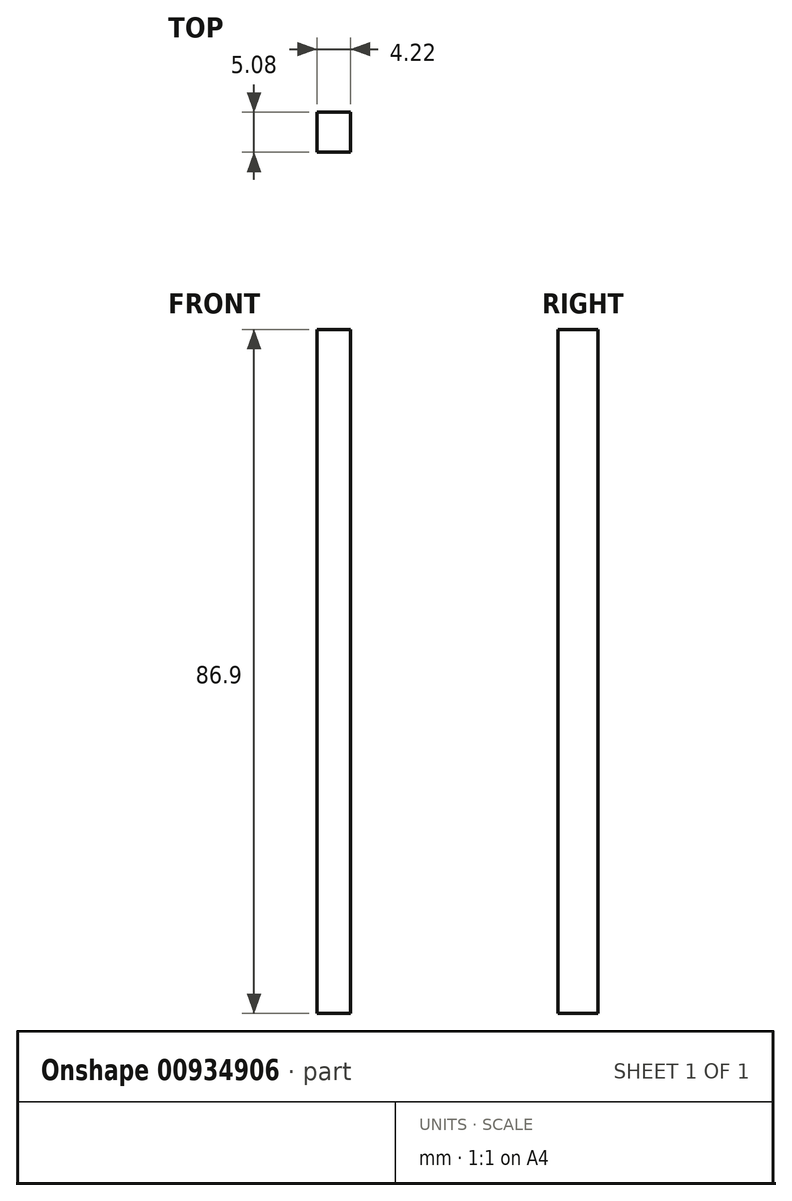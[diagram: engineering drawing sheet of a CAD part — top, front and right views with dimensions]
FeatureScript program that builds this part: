
annotation { "Feature Type Name" : "Feature", "Feature Type Description" : "" }
export const myFeature = defineFeature(function(context is Context, id is Id, definition is map)
    precondition{}
    {
        {
            var Q0;
            Q0=qCreatedBy(makeId("Front.planeOp"),FACE);
            var sketch = newSketch(context, id + "F0", { "sketchPlane" : qUnion([Q0])});
            skLineSegment(sketch, "E0.bottom", {"start": v(0, 0) * mm, "end": v(4.22, 0) * mm});
            skLineSegment(sketch, "E0.top", {"start": v(0, 86.9) * mm, "end": v(4.22, 86.9) * mm});
            skLineSegment(sketch, "E0.left", {"start": v(0, 0) * mm, "end": v(0, 86.9) * mm});
            skLineSegment(sketch, "E0.right", {"start": v(4.22, 0) * mm, "end": v(4.22, 86.9) * mm});
            skSolve(sketch);
        }
        {
            var Q0;
            Q0 = qSketchRegion(id + "F0", true);
            extrude(context, id + "F1", {"entities" : qUnion([Q0]), "depth" : 5.08 * mm, "offsetDistance" : 25.4 * mm});
        }
    });
